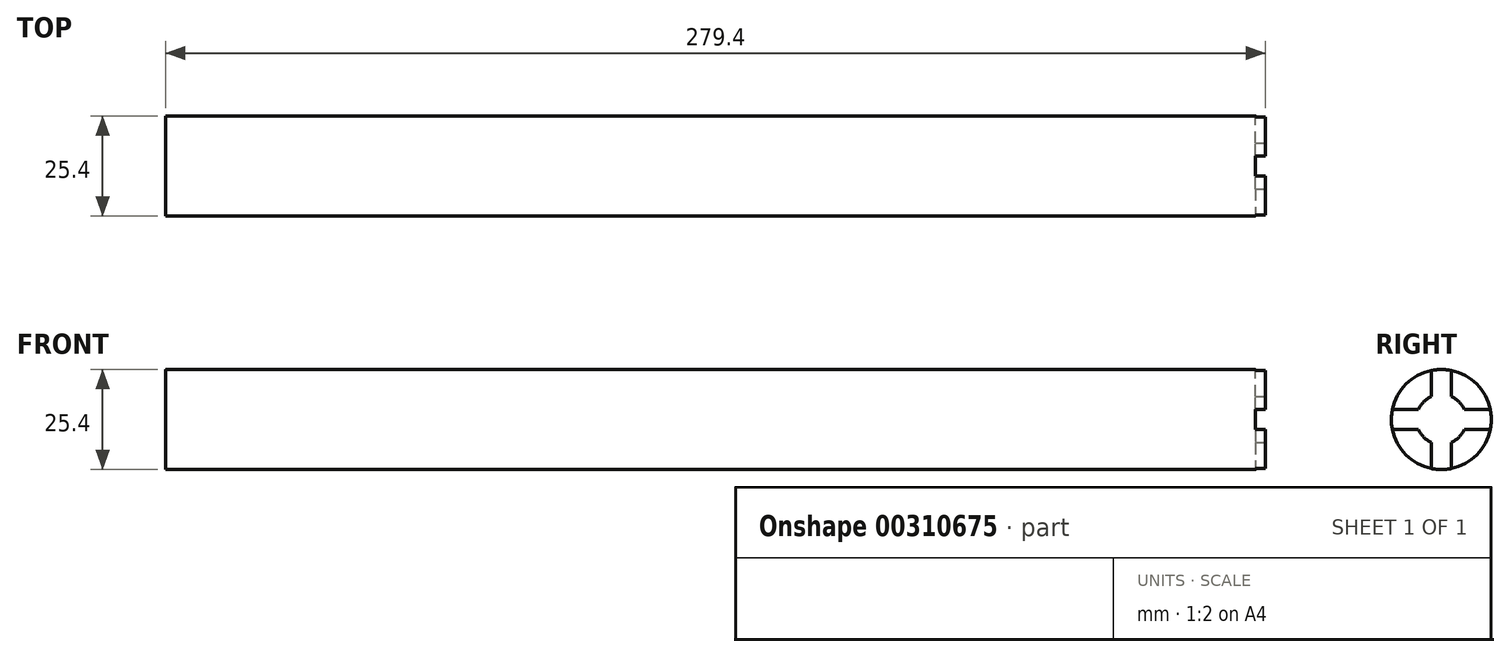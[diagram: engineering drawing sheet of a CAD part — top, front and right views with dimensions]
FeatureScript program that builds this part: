
annotation { "Feature Type Name" : "Feature", "Feature Type Description" : "" }
export const myFeature = defineFeature(function(context is Context, id is Id, definition is map)
    precondition{}
    {
        {
            var Q0;
            Q0=qCreatedBy(makeId("Right.planeOp"),FACE);
            var sketch = newSketch(context, id + "F0", { "sketchPlane" : qUnion([Q0])});
            skCircle(sketch, "E0", {"center": v(0, 0) * mm, "radius": 12.7 * mm});
            skSolve(sketch);
        }
        {
            var Q0;
            Q0 = qSketchRegion(id + "F0", true);
            extrude(context, id + "F1", {"entities" : qUnion([Q0]), "depth" : 279.4 * mm});
        }
        {
            var Q0;
            Q0=makeQuery(id+"F1.opExtrude","CAP_FACE",FACE,{"disambiguationData":[OSD([sQuery(id+"F0.wireOp",EDGE,"E0")])],"isStart":false});
            var sketch = newSketch(context, id + "F2", { "sketchPlane" : qUnion([Q0])});
            skCircle(sketch, "E1", {"center": v(0, 0) * mm, "radius": 6.35 * mm});
            skLineSegment(sketch, "E2", {"start": v(-5.82, -2.54) * mm, "end": v(-12.44, -2.54) * mm});
            skLineSegment(sketch, "E3", {"start": v(-5.82, 2.54) * mm, "end": v(-12.44, 2.54) * mm});
            skLineSegment(sketch, "E4", {"start": v(-2.54, 5.82) * mm, "end": v(-2.54, 12.44) * mm});
            skLineSegment(sketch, "E5", {"start": v(2.54, 5.82) * mm, "end": v(2.54, 12.44) * mm});
            skLineSegment(sketch, "E6", {"start": v(5.82, 2.54) * mm, "end": v(12.44, 2.54) * mm});
            skLineSegment(sketch, "E7", {"start": v(5.82, -2.54) * mm, "end": v(12.44, -2.54) * mm});
            skLineSegment(sketch, "E8", {"start": v(2.54, -5.82) * mm, "end": v(2.54, -12.44) * mm});
            skLineSegment(sketch, "E9", {"start": v(-2.54, -5.82) * mm, "end": v(-2.54, -12.44) * mm});
            skArc(sketch, "E10", {"start": v(-2.54, 12.44) * mm, "mid": v(0, -12.7) * mm, "end": v(2.54, 12.44) * mm});
            skArc(sketch, "E11", {"start": v(12.44, 2.54) * mm, "mid": v(-12.7, 0) * mm, "end": v(12.44, -2.54) * mm});
            skArc(sketch, "E12", {"start": v(2.54, 12.44) * mm, "mid": v(0, 12.7) * mm, "end": v(-2.54, 12.44) * mm});
            skCircle(sketch, "E13", {"center": v(0, 0) * mm, "radius": 12.7 * mm});
            skArc(sketch, "E14", {"start": v(12.44, -2.54) * mm, "mid": v(12.7, 0) * mm, "end": v(12.44, 2.54) * mm});
            skArc(sketch, "E15", {"start": v(-2.54, -12.44) * mm, "mid": v(0, -12.7) * mm, "end": v(2.54, -12.44) * mm});
            skArc(sketch, "E16", {"start": v(-12.44, 2.54) * mm, "mid": v(-12.7, 0) * mm, "end": v(-12.44, -2.54) * mm});
            skSolve(sketch);
        }
        {
            var Q0;
            {var subQ0=sQuery(id+"F2.wireOp",EDGE,"E2");Q0=makeQuery(id+"F2.imprint","IMPRINT",FACE,{"disambiguationData":[TD([[makeQuery(id+"F2.imprint","IMPRINT",EDGE,{"derivedFrom":subQ0}),-1.0]])]});}
            var Q1;
            {var subQ0=sQuery(id+"F2.wireOp",EDGE,"E4");Q1=makeQuery(id+"F2.imprint","IMPRINT",FACE,{"disambiguationData":[TD([[makeQuery(id+"F2.imprint","IMPRINT",EDGE,{"derivedFrom":subQ0}),-1.0]])]});}
            var Q2;
            {var subQ0=sQuery(id+"F2.wireOp",EDGE,"E6");Q2=makeQuery(id+"F2.imprint","IMPRINT",FACE,{"disambiguationData":[TD([[makeQuery(id+"F2.imprint","IMPRINT",EDGE,{"derivedFrom":subQ0}),-1.0]])]});}
            var Q3;
            {var subQ0=sQuery(id+"F2.wireOp",EDGE,"E8");Q3=makeQuery(id+"F2.imprint","IMPRINT",FACE,{"disambiguationData":[TD([[makeQuery(id+"F2.imprint","IMPRINT",EDGE,{"derivedFrom":subQ0}),-1.0]])]});}
            var Q4;
            {var subQ0=sQuery(id+"F2.wireOp",EDGE,"E1");var subQ4=makeQuery(id+"F2.imprint","INTERSECT",VERTEX,{"derivedFrom":[subQ0,sQuery(id+"F2.wireOp",EDGE,"E5")]});Q4=makeQuery(id+"F2.imprint","IMPRINT",FACE,{"disambiguationData":[TD([[makeQuery(id+"F2.imprint","IMPRINT",EDGE,{"disambiguationData":[TD([[subQ4,1.0]])],"derivedFrom":subQ0}),1.0]])]});}
            extrude(context, id + "F3", {"entities" : qUnion([Q0, Q1, Q2, Q3, Q4]), "operationType" : NewBodyOperationType.REMOVE, "oppositeDirection" : true, "depth" : 2.54 * mm});
        }
    });
